FCSTD DOCUMENT  (FreeCAD 1.2R20251230 (Git shallow))
Label: PC_backgroud_GPU
License: All rights reserved
LicenseURL: https://en.wikipedia.org/wiki/All_rights_reserved
objects: App::Point×1, Sketcher::SketchObject×1, PartDesign::Body×1
note: 3 computed .brp shape members not serialized (recipe doc carries the construction recipe); baked Part::Feature solids carry a one-line shape summary decoded from their .brp

FEATURE [App::Point] Origin001  label="原点"
  Role = Origin
FEATURE [Sketcher::SketchObject] Sketch
  ArcFitTolerance = 1e-06
  AttachmentSupport = -> [Origin]
  ExternalTypes = [0]
  FullyConstrained = false
  MakeInternals = false
  MapMode = 5
  sketch-geometry (28):
    g0: LineSegment StartX=0 StartY=0 StartZ=0 EndX=0 EndY=39.5 EndZ=0
    g1: LineSegment StartX=0 StartY=39.5 StartZ=0 EndX=-33.8 EndY=39.5 EndZ=0
    g2: LineSegment StartX=-33.8 StartY=39.5 StartZ=0 EndX=-33.8 EndY=0 EndZ=0
    g3: LineSegment StartX=-33.8 StartY=0 StartZ=0 EndX=0 EndY=0 EndZ=0
    g4: Circle CenterX=-31.05 CenterY=38.5 CenterZ=0 NormalX=0 NormalY=0 NormalZ=1 AngleXU=0 Radius=0.15
    g5: Circle CenterX=-2.75 CenterY=38.5 CenterZ=0 NormalX=0 NormalY=0 NormalZ=1 AngleXU=0 Radius=0.15
    g6: Circle CenterX=-2.75 CenterY=1 CenterZ=0 NormalX=0 NormalY=0 NormalZ=1 AngleXU=0 Radius=0.15
    g7: Circle CenterX=-31.05 CenterY=1 CenterZ=0 NormalX=0 NormalY=0 NormalZ=1 AngleXU=0 Radius=0.15
    g8: LineSegment StartX=-14 StartY=14.5 StartZ=0 EndX=-14 EndY=11.5 EndZ=0
    g9: LineSegment StartX=-14 StartY=11.5 StartZ=0 EndX=-6 EndY=11.5 EndZ=0
    g10: LineSegment StartX=-6 StartY=11.5 StartZ=0 EndX=-6 EndY=14.5 EndZ=0
    g11: LineSegment StartX=-6 StartY=14.5 StartZ=0 EndX=-14 EndY=14.5 EndZ=0
    g12: LineSegment StartX=25.6786 StartY=39.8455 StartZ=0 EndX=25.6786 EndY=0.0455165 EndZ=0
    g13: LineSegment StartX=25.6786 StartY=0.0455165 StartZ=0 EndX=59.4786 EndY=0.0455165 EndZ=0
    g14: LineSegment StartX=59.4786 StartY=0.0455165 StartZ=0 EndX=59.4786 EndY=39.8455 EndZ=0
    g15: LineSegment StartX=59.4786 StartY=39.8455 StartZ=0 EndX=25.6786 EndY=39.8455 EndZ=0
    g16: Circle CenterX=55.1786 CenterY=39.2455 CenterZ=0 NormalX=0 NormalY=0 NormalZ=1 AngleXU=0 Radius=0.165
    g17: Circle CenterX=26.3886 CenterY=36.3655 CenterZ=0 NormalX=0 NormalY=0 NormalZ=1 AngleXU=0 Radius=0.125
    g18: Circle CenterX=26.3886 CenterY=3.65052 CenterZ=0 NormalX=0 NormalY=0 NormalZ=1 AngleXU=0 Radius=0.125
    g19: Circle CenterX=58.8786 CenterY=2.61552 CenterZ=0 NormalX=0 NormalY=0 NormalZ=1 AngleXU=0 Radius=0.165
    g20: LineSegment StartX=34.5786 StartY=28.8455 StartZ=0 EndX=34.5786 EndY=16.3455 EndZ=0
    g21: LineSegment StartX=34.5786 StartY=16.3455 StartZ=0 EndX=41.7786 EndY=16.3455 EndZ=0
    g22: LineSegment StartX=41.7786 StartY=16.3455 StartZ=0 EndX=41.7786 EndY=28.8455 EndZ=0
    g23: LineSegment StartX=41.7786 StartY=28.8455 StartZ=0 EndX=34.5786 EndY=28.8455 EndZ=0
    g24: LineSegment StartX=45.4786 StartY=14.5455 StartZ=0 EndX=45.4786 EndY=11.5455 EndZ=0
    g25: LineSegment StartX=45.4786 StartY=11.5455 StartZ=0 EndX=53.4786 EndY=11.5455 EndZ=0
    g26: LineSegment StartX=53.4786 StartY=11.5455 StartZ=0 EndX=53.4786 EndY=14.5455 EndZ=0
    g27: LineSegment StartX=53.4786 StartY=14.5455 StartZ=0 EndX=45.4786 EndY=14.5455 EndZ=0
  constraints (81):
    c: Coincident(g0,g1)
    c: Coincident(g1,g2)
    c: Coincident(g2,g3)
    c: Coincident(g3,g0)
    c: Vertical(g0)
    c: Vertical(g2)
    c: Horizontal(g1)
    c: Horizontal(g3)
    c: Coincident(g0,g-1)
    c: DistanceX(g1,g1) = 33.8
    c: DistanceY(g2,g2) = 39.5
    c: Diameter(g4) = 0.3
    c: Distance(g4,g1) = 1
    c: Distance(g4,g2) = 2.75
    c: Diameter(g5) = 0.3
    c: Distance(g5,g0) = 2.75
    c: Distance(g5,g1) = 1
    c: Diameter(g7) = 0.3
    c: Distance(g7,g3) = 1
    c: Distance(g7,g2) = 2.75
    c: Diameter(g6) = 0.3
    c: Distance(g6,g3) = 1
    c: DistanceX(g6,g-1) = 2.75
    c: Coincident(g8,g9)
    c: Coincident(g9,g10)
    c: Coincident(g10,g11)
    c: Coincident(g11,g8)
    c: Vertical(g8)
    c: Vertical(g10)
    c: Horizontal(g9)
    c: Horizontal(g11)
    c: DistanceY(g10,g10) = 3
    c: DistanceX(g11,g11) = 8
    c: Distance(g3,g9) = 11.5
    c: Distance(g0,g10) = 6
    c: Coincident(g12,g13)
    c: Coincident(g13,g14)
    c: Coincident(g14,g15)
    c: Coincident(g15,g12)
    c: Vertical(g12)
    c: Vertical(g14)
    c: Horizontal(g13)
    c: Horizontal(g15)
    c: DistanceX(g15,g15) = 33.8
    c: DistanceY(g14,g14) = 39.8
    c: Diameter(g16) = 0.33
    c: Diameter(g19) = 0.33
    c: Diameter(g17) = 0.25
    c: Diameter(g18) = 0.25
    c: Distance(g17,g12) = 0.71
    c: Distance(g18,g12) = 0.71
    c: Distance(g17,g15) = 3.48
    c: Distance(g18,g13) = 3.48
    c: Distance(g19,g14) = 0.6
    c: Distance(g19,g13) = 2.57
    c: Distance(g16,g15) = 0.6
    c: Distance(g16,g14) = 4.3
    c: Coincident(g20,g21)
    c: Coincident(g21,g22)
    c: Coincident(g22,g23)
    c: Coincident(g23,g20)
    c: Vertical(g20)
    c: Vertical(g22)
    c: Horizontal(g21)
    c: Horizontal(g23)
    c: Coincident(g24,g25)
    c: Coincident(g25,g26)
    c: Coincident(g26,g27)
    c: Coincident(g27,g24)
    c: Vertical(g24)
    c: Vertical(g26)
    c: Horizontal(g25)
    c: Horizontal(g27)
    c: DistanceY(g26,g26) = 3
    c: DistanceX(g27,g27) = 8
    c: Distance(g14,g26) = 6
    c: Distance(g13,g25) = 11.5
    c: DistanceY(g20,g20) = 12.5
    c: DistanceX(g23,g23) = 7.2
    c: Distance(g12,g20) = 8.9
    c: Distance(g15,g23) = 11
FEATURE [PartDesign::Body] Body
  AllowCompound = true
  Group = -> [Sketch]
  Origin = -> Origin
